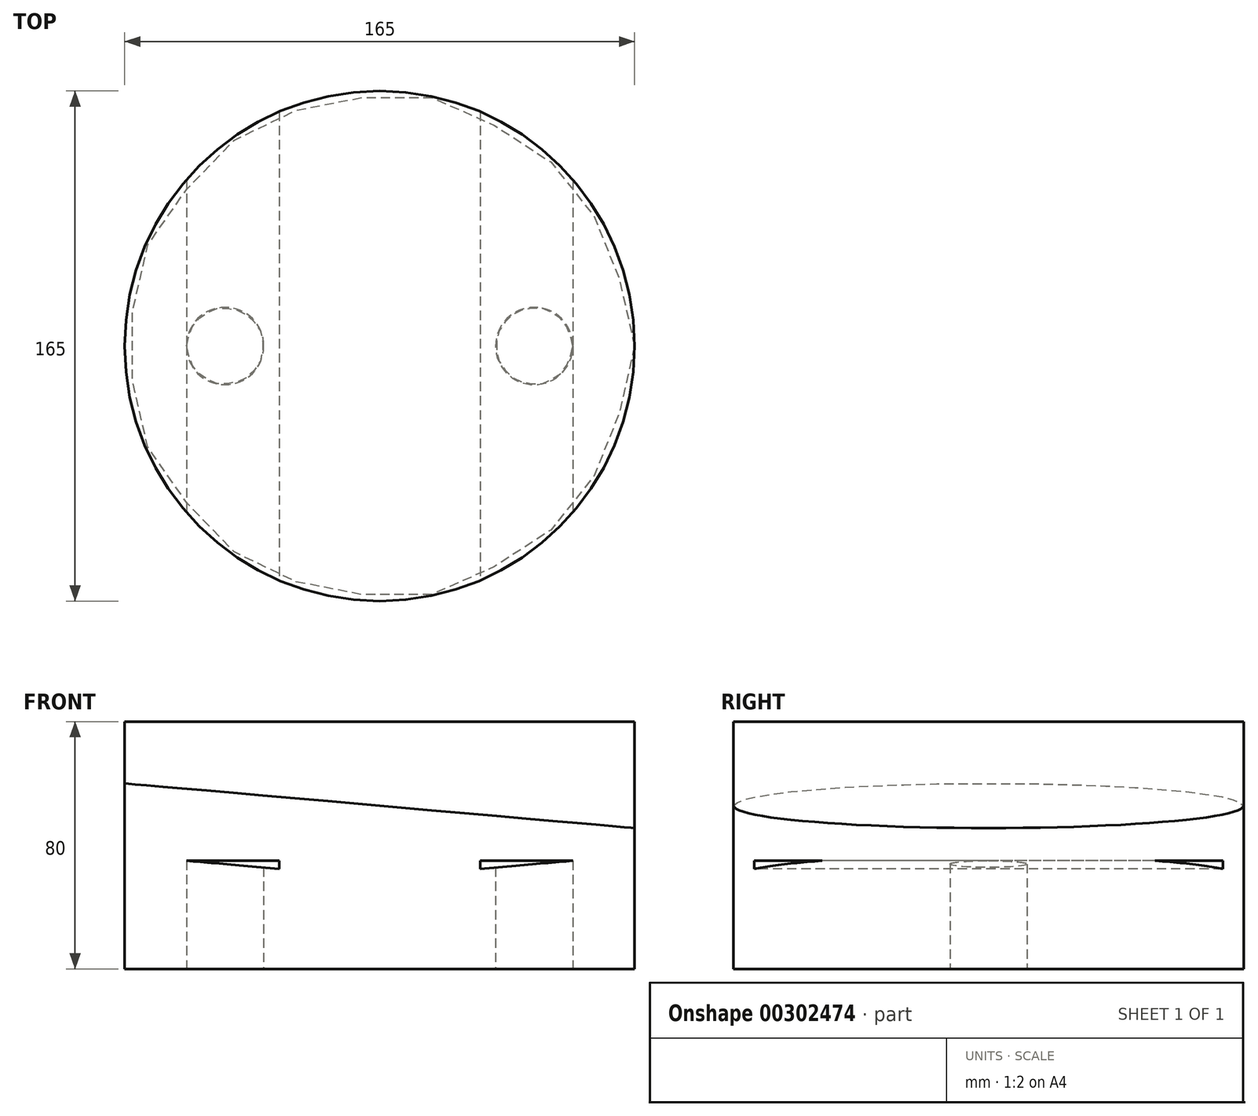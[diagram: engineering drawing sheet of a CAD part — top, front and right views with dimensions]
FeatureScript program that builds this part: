
annotation { "Feature Type Name" : "Feature", "Feature Type Description" : "" }
export const myFeature = defineFeature(function(context is Context, id is Id, definition is map)
    precondition{}
    {
        {
            var Q0;
            Q0=qCreatedBy(makeId("Top.planeOp"),FACE);
            var sketch = newSketch(context, id + "F0", { "sketchPlane" : qUnion([Q0])});
            skCircle(sketch, "E0", {"center": v(0, 0) * mm, "radius": 82.5 * mm});
            skSolve(sketch);
        }
        {
            var Q0;
            Q0 = qSketchRegion(id + "F0", true);
            extrude(context, id + "F1", {"entities" : qUnion([Q0]), "depth" : 60 * mm, "offsetDistance" : 25 * mm});
        }
        {
            var Q0;
            Q0=qCreatedBy(makeId("Top.planeOp"),FACE);
            cPlane(context, id + "F2", {"entities" : qUnion([Q0]), "cplaneType" : CPlaneType.OFFSET, "offset" : 0 * mm, "width" : 152.4 * mm, "height" : 152.4 * mm});
        }
        {
            var Q0;
            Q0=qCreatedBy(id+"F2.planeOp",FACE);
            var sketch = newSketch(context, id + "F3", { "sketchPlane" : qUnion([Q0])});
            skCircle(sketch, "E1", {"center": v(50, 0) * mm, "radius": 12.5 * mm});
            skCircle(sketch, "E2", {"center": v(-50, 0) * mm, "radius": 12.5 * mm});
            skSolve(sketch);
        }
        {
            var Q0;
            Q0 = qSketchRegion(id + "F3", true);
            extrude(context, id + "F4", {"entities" : qUnion([Q0]), "depth" : 35 * mm});
        }
        {
            var Q0;
            Q0=makeQuery(id+"F4.opExtrude","CAP_FACE",FACE,{"disambiguationData":[OSD([sQuery(id+"F3.wireOp",EDGE,"E2")])],"isStart":false});
            var sketch = newSketch(context, id + "F5", { "sketchPlane" : qUnion([Q0])});
            skPoint(sketch, "E3", {"position": v(-62.5, 0) * mm});
            skPoint(sketch, "E4", {"position": v(62.5, 0) * mm});
            skSolve(sketch);
        }
        {
            var Q0;
            Q0=qCreatedBy(makeId("Front.planeOp"),FACE);
            var sketch = newSketch(context, id + "F6", { "sketchPlane" : qUnion([Q0])});
            skLineSegment(sketch, "E5", {"start": v(-62.5, 35) * mm, "end": v(-32.5, 32.38) * mm});
            skLineSegment(sketch, "E6", {"start": v(-32.5, 35) * mm, "end": v(-62.5, 35) * mm});
            skLineSegment(sketch, "E7", {"start": v(62.5, 35) * mm, "end": v(32.5, 32.38) * mm});
            skLineSegment(sketch, "E8", {"start": v(32.5, 35) * mm, "end": v(62.5, 35) * mm});
            skLineSegment(sketch, "E9", {"start": v(-32.5, 35) * mm, "end": v(-32.5, 32.38) * mm});
            skLineSegment(sketch, "E10", {"start": v(32.5, 35) * mm, "end": v(32.5, 32.38) * mm});
            skSolve(sketch);
        }
        {
            var Q0;
            Q0 = qSketchRegion(id + "F6", true);
            extrude(context, id + "F7", {"entities" : qUnion([Q0]), "operationType" : NewBodyOperationType.REMOVE, "endBound" : BoundingType.THROUGH_ALL, "oppositeDirection" : true, "depth" : 25.4 * mm, "hasSecondDirection" : true, "secondDirectionBound" : SecondDirectionBoundingType.THROUGH_ALL, "secondDirectionOppositeDirection" : false, "secondDirectionDepth" : 25.4 * mm, "offsetDistance" : 25 * mm});
        }
        {
            var Q0;
            Q0 = qSketchRegion(id + "F3", true);
            extrude(context, id + "F8", {"entities" : qUnion([Q0]), "operationType" : NewBodyOperationType.REMOVE, "endBound" : BoundingType.UP_TO_NEXT, "depth" : 25 * mm});
        }
        {
            var Q0;
            Q0=makeQuery(id+"F1.opExtrude","CAP_FACE",FACE,{"disambiguationData":[OSD([sQuery(id+"F0.wireOp",EDGE,"E0")])],"isStart":false});
            var sketch = newSketch(context, id + "F9", { "sketchPlane" : qUnion([Q0])});
            skLineSegment(sketch, "E11", {"start": v(-82.5, 0) * mm, "end": v(82.5, 0) * mm});
            skSolve(sketch);
        }
        {
            var Q0;
            Q0=qCreatedBy(makeId("Front.planeOp"),FACE);
            var sketch = newSketch(context, id + "F10", { "sketchPlane" : qUnion([Q0])});
            skLineSegment(sketch, "E12", {"start": v(-82.5, 60) * mm, "end": v(82.5, 45.56) * mm});
            skLineSegment(sketch, "E13", {"start": v(82.5, 60) * mm, "end": v(82.5, 45.56) * mm});
            skLineSegment(sketch, "E14", {"start": v(-82.5, 60) * mm, "end": v(82.5, 60) * mm});
            skSolve(sketch);
        }
        {
            var Q0;
            Q0 = qSketchRegion(id + "F10", true);
            extrude(context, id + "F11", {"entities" : qUnion([Q0]), "operationType" : NewBodyOperationType.REMOVE, "endBound" : BoundingType.THROUGH_ALL, "oppositeDirection" : true, "depth" : 25 * mm, "offsetDistance" : 25 * mm, "hasSecondDirection" : true, "secondDirectionBound" : SecondDirectionBoundingType.THROUGH_ALL, "secondDirectionOppositeDirection" : false, "secondDirectionDepth" : 25 * mm});
        }
        {
            var Q0;
            {var subQ0=sQuery(id+"F9.wireOp",EDGE,"E11");Q0=makeQuery(id+"F9.imprint","IMPRINT",FACE,{"disambiguationData":[TD([[makeQuery(id+"F9.imprint","IMPRINT",EDGE,{"derivedFrom":subQ0}),1.0]])]});}
            var Q1;
            {var subQ0=sQuery(id+"F9.wireOp",EDGE,"E11");Q1=makeQuery(id+"F9.imprint","IMPRINT",FACE,{"disambiguationData":[TD([[makeQuery(id+"F9.imprint","IMPRINT",EDGE,{"derivedFrom":subQ0}),-1.0]])]});}
            var Q2;
            Q2=makeQuery(id+"F11.boolean.opBoolean","COPY",FACE,{"derivedFrom":makeQuery(id+"F11.opExtrude","SWEPT_FACE",FACE,{"disambiguationData":[OSD([sQuery(id+"F10.wireOp",EDGE,"E12")])]})});
            extrude(context, id + "F12", {"entities" : qUnion([Q0, Q1]), "depth" : 20 * mm, "offsetDistance" : 25 * mm, "hasSecondDirection" : true, "secondDirectionBound" : SecondDirectionBoundingType.UP_TO_SURFACE, "secondDirectionOppositeDirection" : true, "secondDirectionDepth" : 25 * mm, "secondDirectionBoundEntityFace" : qUnion([Q2])});
        }
    });
